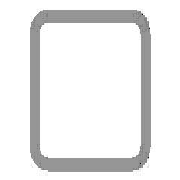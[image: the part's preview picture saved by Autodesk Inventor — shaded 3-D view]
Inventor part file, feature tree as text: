
AUTODESK INVENTOR PART (.ipt)
format: ipt  version: 2025 (Build 290162010, 162A)  size: 134,656 bytes
history: native  units: mm (DEFAULTED — no unit token found)
features: other x4, sketch x1, plane x1
ambient origin geometry x8: Origin, YZ Plane, XZ Plane, XY Plane, X Axis, Y Axis, Z Axis, Center Point
bodies: Solid1 (feature_tree), Body (feature_tree)
feature tree (6):
  parser-record x1  (decoder bookkeeping rows leaked as tree rows — omitted from the tree; the rows remain in map.json)
  other  "Driven Length"
  other  "Start Plane"
  other  "End Plane"
  sketch  "Sketch3"  dims[d3=600.0mm d4=0.0mm d7=4.0mm d9=40.0mm d11=40.0mm d12=2.0mm d13=20.0mm d14=620.0mm d15=20.0mm d16=20.0mm d17=90.0deg d18=600.0mm]
  plane  "Work Plane3"
